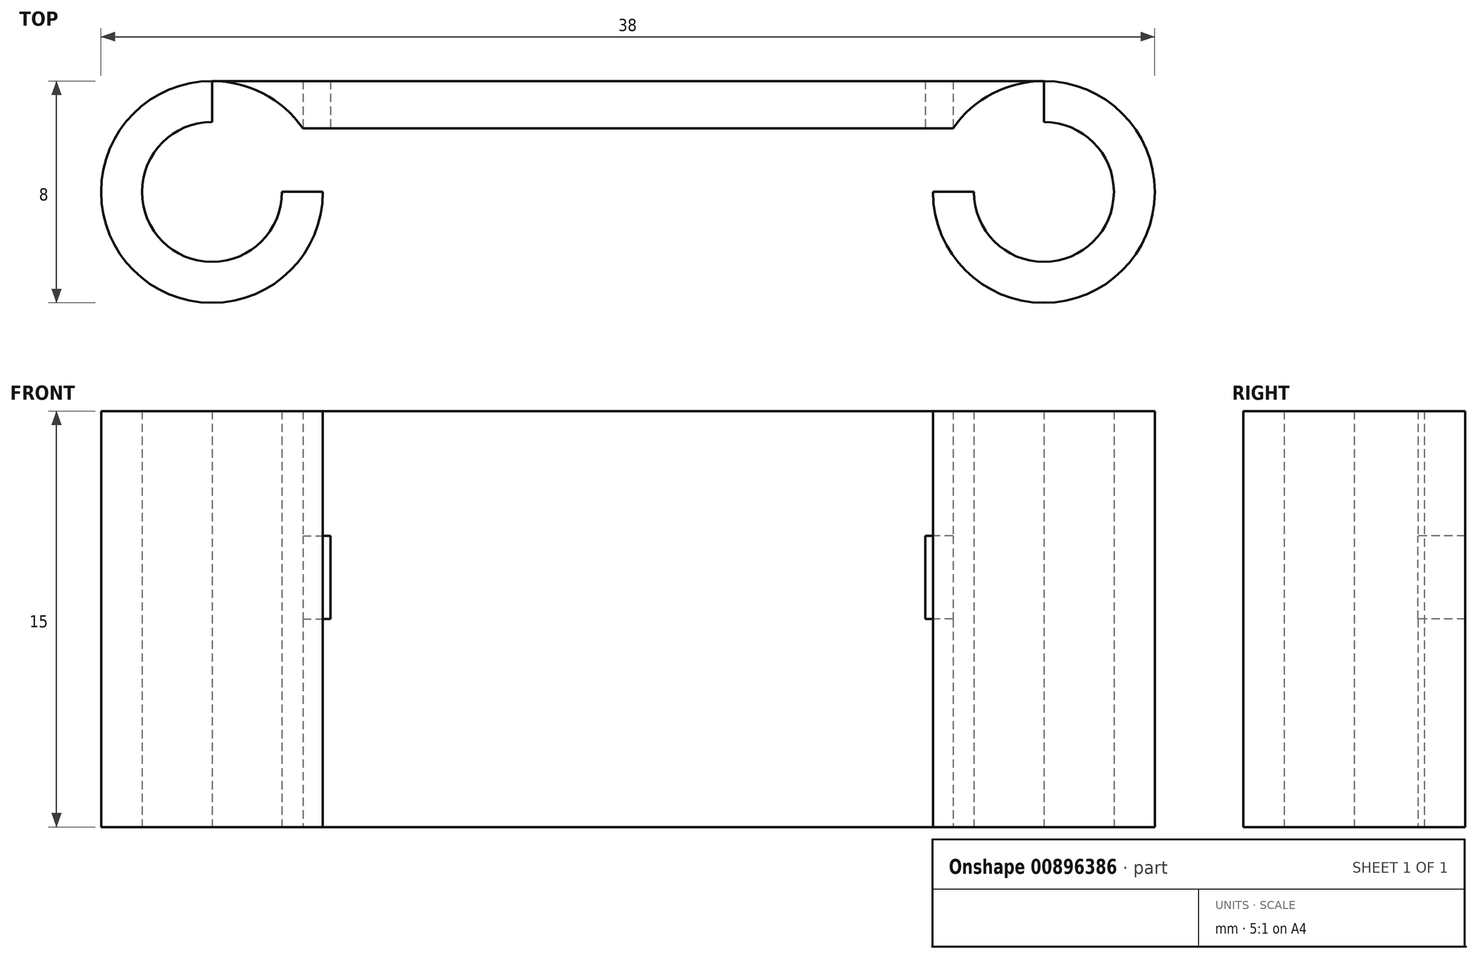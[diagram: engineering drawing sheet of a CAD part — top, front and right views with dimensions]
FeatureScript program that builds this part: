
annotation { "Feature Type Name" : "Feature", "Feature Type Description" : "" }
export const myFeature = defineFeature(function(context is Context, id is Id, definition is map)
    precondition{}
    {
        {
            var Q0;
            Q0=qCreatedBy(makeId("Top.planeOp"),FACE);
            var sketch = newSketch(context, id + "F0", { "sketchPlane" : qUnion([Q0])});
            skCircle(sketch, "E0", {"center": v(-18.46, 0) * mm, "radius": 2.52 * mm});
            skCircle(sketch, "E1", {"center": v(11.54, 0) * mm, "radius": 2.52 * mm});
            skCircle(sketch, "E2", {"center": v(-18.46, 0) * mm, "radius": 4 * mm});
            skCircle(sketch, "E3", {"center": v(11.54, 0) * mm, "radius": 4 * mm});
            skLineSegment(sketch, "E4.bottom", {"start": v(-18.46, 0) * mm, "end": v(11.54, 0) * mm});
            skLineSegment(sketch, "E4.top", {"start": v(-18.46, 0) * mm, "end": v(11.54, 0) * mm});
            skLineSegment(sketch, "E4.left", {"start": v(-18.46, 0) * mm, "end": v(-18.46, 0) * mm});
            skLineSegment(sketch, "E4.right", {"start": v(11.54, 0) * mm, "end": v(11.54, 0) * mm});
            skLineSegment(sketch, "E5.bottom", {"start": v(11.54, 4) * mm, "end": v(-18.46, 4) * mm});
            skLineSegment(sketch, "E5.top", {"start": v(11.54, 0) * mm, "end": v(-18.46, 0) * mm});
            skLineSegment(sketch, "E5.left", {"start": v(11.54, 4) * mm, "end": v(11.54, 0) * mm});
            skLineSegment(sketch, "E5.right", {"start": v(-18.46, 4) * mm, "end": v(-18.46, 0) * mm});
            skLineSegment(sketch, "E6.bottom", {"start": v(-12.3, 0) * mm, "end": v(6.27, 0) * mm});
            skLineSegment(sketch, "E6.top", {"start": v(-12.3, 2.3) * mm, "end": v(6.27, 2.3) * mm});
            skLineSegment(sketch, "E6.left", {"start": v(-12.3, 0) * mm, "end": v(-12.3, 2.3) * mm});
            skLineSegment(sketch, "E6.right", {"start": v(6.27, 0) * mm, "end": v(6.27, 2.3) * mm});
            skLineSegment(sketch, "E7", {"start": v(-12.3, 2.3) * mm, "end": v(8.27, 2.3) * mm});
            skLineSegment(sketch, "E8", {"start": v(8.27, 2.3) * mm, "end": v(-12.3, 2.3) * mm});
            skLineSegment(sketch, "E9", {"start": v(-12.3, 2.3) * mm, "end": v(-15.18, 2.3) * mm});
            skSolve(sketch);
        }
        {
            var Q0;
            {var subQ0=sQuery(id+"F0.wireOp",EDGE,"E5.top");var subQ1=sQuery(id+"F0.wireOp",EDGE,"E0");var subQ2=makeQuery(id+"F0.imprint","INTERSECT",VERTEX,{"derivedFrom":[subQ1,subQ0]});Q0=makeQuery(id+"F0.imprint","IMPRINT",FACE,{"disambiguationData":[TD([[makeQuery(id+"F0.imprint","IMPRINT",EDGE,{"disambiguationData":[TD([[subQ2,1.0]])],"derivedFrom":subQ1}),-1.0]])]});}
            var Q1;
            {var subQ0=sQuery(id+"F0.wireOp",EDGE,"E5.top");var subQ1=sQuery(id+"F0.wireOp",EDGE,"E1");var subQ2=makeQuery(id+"F0.imprint","INTERSECT",VERTEX,{"derivedFrom":[subQ1,subQ0]});Q1=makeQuery(id+"F0.imprint","IMPRINT",FACE,{"disambiguationData":[TD([[makeQuery(id+"F0.imprint","IMPRINT",EDGE,{"disambiguationData":[TD([[subQ2,-1.0]])],"derivedFrom":subQ1}),-1.0]])]});}
            var Q2;
            {var subQ2=sQuery(id+"F0.wireOp",EDGE,"E5.top");var subQ4=sQuery(id+"F0.wireOp",EDGE,"E0");var subQ5=makeQuery(id+"F0.imprint","INTERSECT",VERTEX,{"derivedFrom":[subQ4,subQ2]});Q2=makeQuery(id+"F0.imprint","IMPRINT",FACE,{"disambiguationData":[TD([[makeQuery(id+"F0.imprint","IMPRINT",EDGE,{"disambiguationData":[TD([[subQ5,-1.0]])],"derivedFrom":subQ4}),-1.0]])]});}
            var Q3;
            {var subQ2=sQuery(id+"F0.wireOp",EDGE,"E5.top");var subQ4=sQuery(id+"F0.wireOp",EDGE,"E1");var subQ5=makeQuery(id+"F0.imprint","INTERSECT",VERTEX,{"derivedFrom":[subQ4,subQ2]});Q3=makeQuery(id+"F0.imprint","IMPRINT",FACE,{"disambiguationData":[TD([[makeQuery(id+"F0.imprint","IMPRINT",EDGE,{"disambiguationData":[TD([[subQ5,1.0]])],"derivedFrom":subQ4}),-1.0]])]});}
            var Q4;
            {var subQ4=sQuery(id+"F0.wireOp",EDGE,"E5.bottom");Q4=makeQuery(id+"F0.imprint","IMPRINT",FACE,{"disambiguationData":[TD([[makeQuery(id+"F0.imprint","IMPRINT",EDGE,{"derivedFrom":subQ4}),1.0]])]});}
            extrude(context, id + "F1", {"entities" : qUnion([Q0, Q1, Q2, Q3, Q4]), "depth" : 15 * mm, "offsetDistance" : 25 * mm});
        }
        {
            var Q0;
            Q0=makeQuery(id+"F1.opExtrude","SWEPT_FACE",FACE,{"disambiguationData":[OSD([sQuery(id+"F0.wireOp",EDGE,"E8"),sQuery(id+"F0.wireOp",EDGE,"E9")])]});
            var sketch = newSketch(context, id + "F2", { "sketchPlane" : qUnion([Q0])});
            skLineSegment(sketch, "E10.bottom", {"start": v(-15.18, 7.5) * mm, "end": v(-14.18, 7.5) * mm});
            skLineSegment(sketch, "E10.top", {"start": v(-15.18, 10.5) * mm, "end": v(-14.18, 10.5) * mm});
            skLineSegment(sketch, "E10.left", {"start": v(-15.18, 7.5) * mm, "end": v(-15.18, 10.5) * mm});
            skLineSegment(sketch, "E10.right", {"start": v(-14.18, 7.5) * mm, "end": v(-14.18, 10.5) * mm});
            skLineSegment(sketch, "E11.bottom", {"start": v(8.27, 7.5) * mm, "end": v(7.27, 7.5) * mm});
            skLineSegment(sketch, "E11.top", {"start": v(8.27, 10.5) * mm, "end": v(7.27, 10.5) * mm});
            skLineSegment(sketch, "E11.left", {"start": v(8.27, 7.5) * mm, "end": v(8.27, 10.5) * mm});
            skLineSegment(sketch, "E11.right", {"start": v(7.27, 7.5) * mm, "end": v(7.27, 10.5) * mm});
            skSolve(sketch);
        }
        {
            var Q0;
            Q0 = qSketchRegion(id + "F2", true);
            extrude(context, id + "F3", {"entities" : qUnion([Q0]), "operationType" : NewBodyOperationType.REMOVE, "oppositeDirection" : true, "depth" : 25 * mm, "offsetDistance" : 25 * mm});
        }
    });
